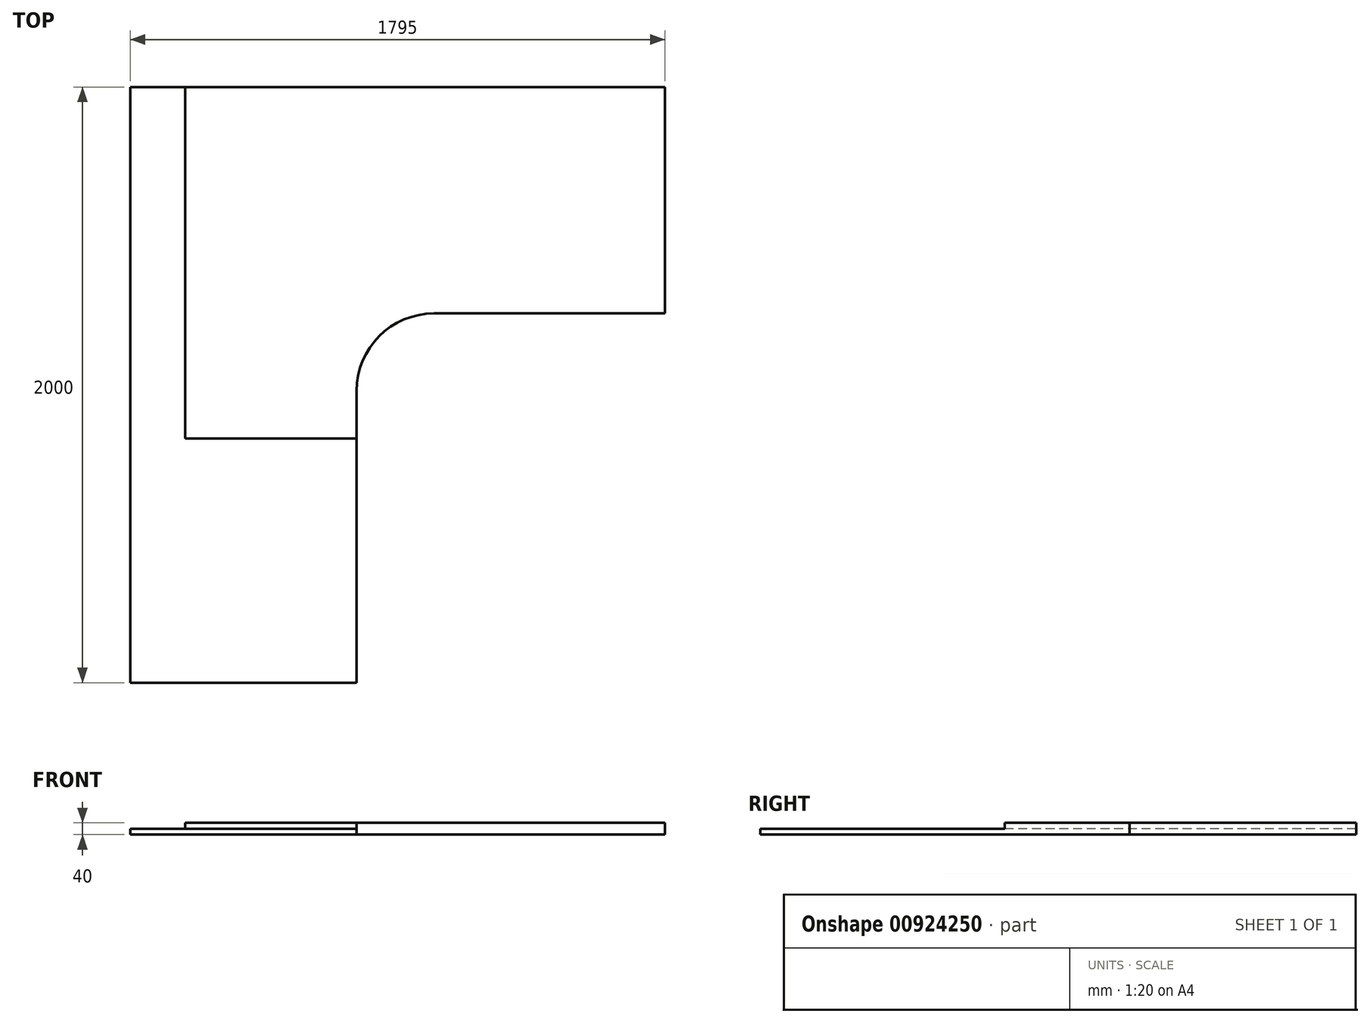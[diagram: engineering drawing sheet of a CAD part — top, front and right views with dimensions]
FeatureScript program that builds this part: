
annotation { "Feature Type Name" : "Feature", "Feature Type Description" : "" }
export const myFeature = defineFeature(function(context is Context, id is Id, definition is map)
    precondition{}
    {
        {
            assignVariable(context, id + "F0", {"name" : "hL", "anyValue" : 970});
        }
        {
            assignVariable(context, id + "F1", {"name" : "hd", "anyValue" : 740});
        }
        {
            var Q0;
            Q0=qCreatedBy(makeId("Top.planeOp"),FACE);
            var sketch = newSketch(context, id + "F2", { "sketchPlane" : qUnion([Q0])});
            skLineSegment(sketch, "E0.bottom", {"start": v(-760, 760) * mm, "end": v(1035, 760) * mm});
            skLineSegment(sketch, "E0.top", {"start": v(-760, -1240) * mm, "end": v(1035, -1240) * mm});
            skLineSegment(sketch, "E0.left", {"start": v(-760, 760) * mm, "end": v(-760, -1240) * mm});
            skLineSegment(sketch, "E0.right", {"start": v(1035, 760) * mm, "end": v(1035, -1240) * mm});
            skSolve(sketch);
        }
        {
            var Q0;
            Q0=qCreatedBy(makeId("Top.planeOp"),FACE);
            cPlane(context, id + "F3", {"entities" : qUnion([Q0]), "cplaneType" : CPlaneType.OFFSET, "offset" : (getVariable(context, 'hd') - 20) * mm, "width" : 150 * mm, "height" : 150 * mm});
        }
        {
            var Q0;
            Q0=qCreatedBy(id+"F3.planeOp",FACE);
            var sketch = newSketch(context, id + "F4", { "sketchPlane" : qUnion([Q0])});
            skPoint(sketch, "E1.0", {"position": v(1035, 760) * mm});
            skPoint(sketch, "E2.0", {"position": v(-760, 760) * mm});
            skPoint(sketch, "E3.0", {"position": v(-760, -1240) * mm});
            skLineSegment(sketch, "E4", {"start": v(260, 0) * mm, "end": v(1035, 0) * mm});
            skLineSegment(sketch, "E5", {"start": v(1035, 0) * mm, "end": v(1035, 760) * mm});
            skLineSegment(sketch, "E6", {"start": v(-760, 760) * mm, "end": v(-760, -1240) * mm});
            skLineSegment(sketch, "E7", {"start": v(0, -1240) * mm, "end": v(0, -260) * mm});
            skLineSegment(sketch, "E8", {"start": v(-760, 760) * mm, "end": v(1035, 760) * mm});
            skLineSegment(sketch, "E9", {"start": v(-760, -1240) * mm, "end": v(0, -1240) * mm});
            skPoint(sketch, "E10.visualSharp", {"position": v(0, 0) * mm});
            skArc(sketch, "E10.filletArc", {"start": v(260, 0) * mm, "mid": v(76.15, -76.15) * mm, "end": v(0, -260) * mm});
            skLineSegment(sketch, "E11", {"start": v(-575, 760) * mm, "end": v(-575, -420) * mm});
            skLineSegment(sketch, "E12", {"start": v(-575, -420) * mm, "end": v(0, -420) * mm});
            skSolve(sketch);
        }
        {
            var Q0;
            Q0=makeQuery(id+"F4.imprint","IMPRINT",FACE,{"disambiguationData":[TD([[makeQuery(id+"F4.imprint","IMPRINT",EDGE,{"derivedFrom":sQuery(id+"F4.wireOp",EDGE,"E4")}),1.0]])]});
            extrude(context, id + "F5", {"entities" : qUnion([Q0]), "depth" : 20 * mm, "offsetDistance" : 25 * mm});
        }
        {
            var Q0;
            Q0=qSketchRegion(id+"F4",true);
            extrude(context, id + "F6", {"entities" : qUnion([Q0]), "operationType" : NewBodyOperationType.ADD, "oppositeDirection" : true, "depth" : 20 * mm, "offsetDistance" : 25 * mm});
        }
        {
            var Q0;
            Q0=qCreatedBy(makeId("Top.planeOp"),FACE);
            cPlane(context, id + "F7", {"entities" : qUnion([Q0]), "cplaneType" : CPlaneType.OFFSET, "offset" : (getVariable(context, 'hd') + getVariable(context, 'hL')) * mm, "width" : 150 * mm, "height" : 150 * mm});
        }
        {
            var Q0;
            Q0=qCreatedBy(id+"F7.planeOp",FACE);
            var sketch = newSketch(context, id + "F8", { "sketchPlane" : qUnion([Q0])});
            skPoint(sketch, "E13", {"position": v(-300, -300) * mm});
            skPoint(sketch, "E14", {"position": v(300, 300) * mm});
            skPoint(sketch, "E15.0", {"position": v(260, -260) * mm});
            skArc(sketch, "E16.0", {"start": v(260, 300) * mm, "mid": v(-135.98, 135.98) * mm, "end": v(-300, -260) * mm, "construction": true});
            skPoint(sketch, "E17.0", {"position": v(-760, 760) * mm});
            skLineSegment(sketch, "E18", {"start": v(-760, 760) * mm, "end": v(260, -260) * mm, "construction": true});
            skPoint(sketch, "E19", {"position": v(-135.98, 135.98) * mm});
            skPoint(sketch, "E20", {"position": v(750, 300) * mm});
            skSolve(sketch);
        }
        {
            var Q0;
            Q0=qCreatedBy(makeId("Top.planeOp"),FACE);
            var sketch = newSketch(context, id + "F9", { "sketchPlane" : qUnion([Q0])});
            skPoint(sketch, "E21.0", {"position": v(-135.98, 135.98) * mm});
            skCircle(sketch, "E22", {"center": v(-135.98, 135.98) * mm, "radius": 555.61 * mm});
            skPoint(sketch, "E23.0", {"position": v(300, 300) * mm});
            skPoint(sketch, "E24.0", {"position": v(-300, -300) * mm});
            skCircle(sketch, "E25", {"center": v(300, 300) * mm, "radius": 555.61 * mm});
            skCircle(sketch, "E26", {"center": v(-300, -300) * mm, "radius": 555.61 * mm});
            skPoint(sketch, "E27.0", {"position": v(750, 300) * mm});
            skCircle(sketch, "E28", {"center": v(750, 300) * mm, "radius": 555.61 * mm});
            skSolve(sketch);
        }
        {
            var Q0;
            Q0=makeQuery(id+"F9.imprint","IMPRINT",FACE,{"disambiguationData":[TD([[makeQuery(id+"F9.imprint","IMPRINT",EDGE,{"derivedFrom":sQuery(id+"F9.wireOp",EDGE,"E22")}),1.0]])]});
            var Q1;
            Q1=sQuery(id+"F8.wireOp",VERTEX,"cbbe6bf4-1df4-4786-b697-ca3d39312b80");
            var Q2;
            Q2=sQuery(id+"F9.wireOp",EDGE,"E22");
            var Q3;
            Q3=sQuery(id+"F8.wireOp",VERTEX,"E19");
            loft(context, id + "F10", {"bodyType" : ToolBodyType.SURFACE, "sheetProfilesArray" : [{ "sheetProfileEntities" : qUnion([Q0]) }, { "sheetProfileEntities" : qUnion([Q1]) }], "wireProfilesArray" : [{ "wireProfileEntities" : qUnion([Q2]) }, { "wireProfileEntities" : qUnion([Q3]) }]});
        }
        {
            var Q1;
            {var subQ0=sQuery(id+"F9.wireOp",EDGE,"E25");var subQ1=sQuery(id+"F9.wireOp",EDGE,"E22");var subQ2=makeQuery(id+"F9.imprint","INTERSECT",VERTEX,{"disambiguationData":[OD(0.0)],"derivedFrom":[subQ1,subQ0]});Q1=makeQuery(id+"F9.imprint","IMPRINT",FACE,{"disambiguationData":[TD([[makeQuery(id+"F9.imprint","IMPRINT",EDGE,{"disambiguationData":[TD([[subQ2,1.0]])],"derivedFrom":subQ1}),-1.0]])]});}
            var Q2;
            {var subQ0=sQuery(id+"F9.wireOp",EDGE,"E25");var subQ1=sQuery(id+"F9.wireOp",EDGE,"E22");var subQ2=makeQuery(id+"F9.imprint","INTERSECT",VERTEX,{"disambiguationData":[OD(1.0)],"derivedFrom":[subQ1,subQ0]});Q2=makeQuery(id+"F9.imprint","IMPRINT",FACE,{"disambiguationData":[TD([[makeQuery(id+"F9.imprint","IMPRINT",EDGE,{"disambiguationData":[TD([[subQ2,-1.0]])],"derivedFrom":subQ1}),1.0]])]});}
            var Q3;
            {var subQ0=sQuery(id+"F9.wireOp",EDGE,"E25");var subQ1=sQuery(id+"F9.wireOp",EDGE,"E22");var subQ2=makeQuery(id+"F9.imprint","INTERSECT",VERTEX,{"disambiguationData":[OD(0.0)],"derivedFrom":[subQ1,subQ0]});Q3=makeQuery(id+"F9.imprint","IMPRINT",FACE,{"disambiguationData":[TD([[makeQuery(id+"F9.imprint","IMPRINT",EDGE,{"disambiguationData":[TD([[subQ2,1.0]])],"derivedFrom":subQ1}),1.0]])]});}
            var Q4;
            Q4=sQuery(id+"F8.wireOp",VERTEX,"E14");
            var Q5;
            Q5=sQuery(id+"F9.wireOp",EDGE,"E25");
            var Q6;
            Q6=sQuery(id+"F8.wireOp",VERTEX,"E14");
            loft(context, id + "F11", {"bodyType" : ToolBodyType.SURFACE, "sheetProfilesArray" : [{ "sheetProfileEntities" : qUnion([Q1]) }, { "sheetProfileEntities" : qUnion([Q2]) }, { "sheetProfileEntities" : qUnion([Q3]) }, { "sheetProfileEntities" : qUnion([Q4]) }], "wireProfilesArray" : [{ "wireProfileEntities" : qUnion([Q5]) }, { "wireProfileEntities" : qUnion([Q6]) }]});
        }
        {
            var Q0;
            Q0=sQuery(id+"F9.wireOp",EDGE,"E26");
            var Q1;
            Q1=sQuery(id+"F8.wireOp",VERTEX,"E13");
            loft(context, id + "F12", {"bodyType" : ToolBodyType.SURFACE, "wireProfilesArray" : [{ "wireProfileEntities" : qUnion([Q0]) }, { "wireProfileEntities" : qUnion([Q1]) }]});
        }
        {
            var Q0;
            Q0=sQuery(id+"F9.wireOp",EDGE,"E28");
            var Q1;
            Q1=sQuery(id+"F8.wireOp",VERTEX,"E20");
            loft(context, id + "F13", {"bodyType" : ToolBodyType.SURFACE, "wireProfilesArray" : [{ "wireProfileEntities" : qUnion([Q0]) }, { "wireProfileEntities" : qUnion([Q1]) }]});
        }
    });
